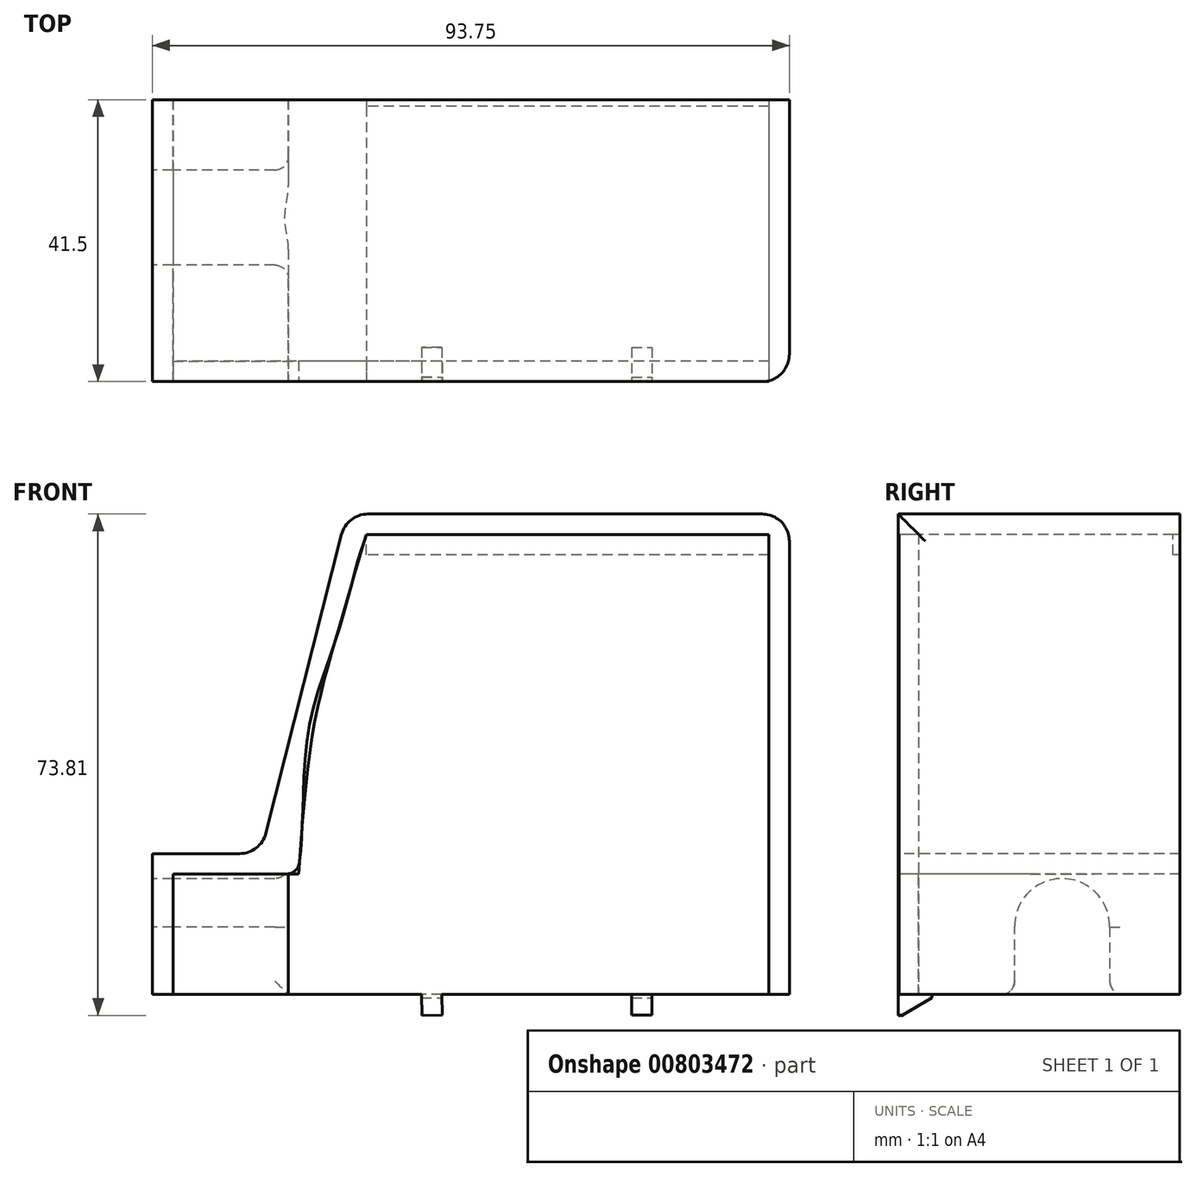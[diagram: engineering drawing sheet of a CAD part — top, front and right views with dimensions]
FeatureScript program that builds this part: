
annotation { "Feature Type Name" : "Feature", "Feature Type Description" : "" }
export const myFeature = defineFeature(function(context is Context, id is Id, definition is map)
    precondition{}
    {
        {
            var Q0;
            Q0=qCreatedBy(makeId("Front.planeOp"),FACE);
            var sketch = newSketch(context, id + "F0", { "sketchPlane" : qUnion([Q0])});
            skLineSegment(sketch, "E0", {"start": v(59.25, 24.1) * mm, "end": v(0, 24.1) * mm});
            skFitSpline(sketch, "E1", {"points": [v(0, 24.1) * mm, v(-4.07, 10.26) * mm, v(-7.71, -4.08) * mm, v(-10, -25.9) * mm], "startDerivative": vector(-13.66, -42.75) * mm, "endDerivative": vector(-4.48, -59.85) * mm});
            skLineSegment(sketch, "E2", {"start": v(59.26, -43.65) * mm, "end": v(-28.5, -43.65) * mm});
            skLineSegment(sketch, "E3", {"start": v(-28.5, -43.65) * mm, "end": v(-28.5, -25.9) * mm});
            skLineSegment(sketch, "E4", {"start": v(-28.5, -25.9) * mm, "end": v(-10, -25.9) * mm});
            skLineSegment(sketch, "E5", {"start": v(59.25, 24.1) * mm, "end": v(59.26, -43.65) * mm});
            skSolve(sketch);
        }
        {
            var Q0;
            Q0 = qSketchRegion(id + "F0", true);
            extrude(context, id + "F1", {"entities" : qUnion([Q0]), "oppositeDirection" : true, "depth" : 3 * mm, "offsetDistance" : 25 * mm});
        }
        {
            var Q0;
            Q0=makeQuery(id+"F0.imprint","IMPRINT",FACE,{"disambiguationData":[TD([[makeQuery(id+"F0.imprint","IMPRINT",EDGE,{"derivedFrom":sQuery(id+"F0.wireOp",EDGE,"E0")}),1.0]])]});
            var Q1;
            Q1 = qBodyType(qCreatedBy(id + "Fs2WI9H54nxdFtR_1" ,EDGE), BodyType.WIRE);
            cPlane(context, id + "F2", {"entities" : qUnion([Q0, Q1]), "cplaneType" : CPlaneType.OFFSET, "offset" : 0 * mm, "width" : 150 * mm, "height" : 150 * mm});
        }
        {
            var Q0;
            Q0=qCreatedBy(id+"F2.planeOp",FACE);
            var sketch = newSketch(context, id + "F3", { "sketchPlane" : qUnion([Q0])});
            skLineSegment(sketch, "E6.0.0", {"start": v(-28.5, -25.9) * mm, "end": v(-28.5, -43.65) * mm});
            skLineSegment(sketch, "E6.0.2", {"start": v(59.26, -43.65) * mm, "end": v(59.25, 24.1) * mm});
            skLineSegment(sketch, "E6.0.3", {"start": v(59.25, 24.1) * mm, "end": v(0, 24.1) * mm});
            skFitSpline(sketch, "E6.0.4", {"points": [v(0, 24.1) * mm, v(-1.4, 19.7) * mm, v(-4.08, 9.94) * mm, v(-8.4, -4.13) * mm, v(-9.43, -18.32) * mm, v(-10, -25.9) * mm]});
            skLineSegment(sketch, "E6.0.5", {"start": v(-10, -25.9) * mm, "end": v(-28.5, -25.9) * mm});
            skLineSegment(sketch, "E7", {"start": v(-28.5, -43.65) * mm, "end": v(-31.5, -43.65) * mm});
            skLineSegment(sketch, "E8", {"start": v(-31.5, -43.65) * mm, "end": v(-31.5, -22.9) * mm});
            skLineSegment(sketch, "E9", {"start": v(-31.5, -22.9) * mm, "end": v(-15.56, -22.9) * mm});
            skLineSegment(sketch, "E10", {"start": v(-15.56, -22.9) * mm, "end": v(-2.92, 27.1) * mm});
            skLineSegment(sketch, "E11", {"start": v(-2.92, 27.1) * mm, "end": v(62.26, 27.1) * mm});
            skLineSegment(sketch, "E12", {"start": v(62.26, 27.1) * mm, "end": v(62.26, -43.65) * mm});
            skLineSegment(sketch, "E13", {"start": v(62.26, -43.65) * mm, "end": v(59.26, -43.65) * mm});
            skSolve(sketch);
        }
        {
            var Q0;
            Q0 = qSketchRegion(id + "F3", true);
            extrude(context, id + "F4", {"entities" : qUnion([Q0]), "oppositeDirection" : true, "depth" : 41.5 * mm, "offsetDistance" : 25 * mm});
        }
        {
            var Q0;
            Q0=makeQuery(id+"F4.opExtrude","SWEPT_FACE",FACE,{"disambiguationData":[OSD([sQuery(id+"F3.wireOp",EDGE,"E8")])]});
            cPlane(context, id + "F5", {"entities" : qUnion([Q0]), "cplaneType" : CPlaneType.OFFSET, "offset" : 0 * mm, "width" : 150 * mm, "height" : 150 * mm});
        }
        {
            var Q0;
            Q0=qCreatedBy(id+"F5.planeOp",FACE);
            var sketch = newSketch(context, id + "F6", { "sketchPlane" : qUnion([Q0])});
            skArc(sketch, "E14", {"start": v(-17.15, -33.62) * mm, "mid": v(-24.19, -26.58) * mm, "end": v(-31.15, -33.7) * mm});
            skLineSegment(sketch, "E15", {"start": v(-17.15, -33.62) * mm, "end": v(-17.15, -53.22) * mm});
            skLineSegment(sketch, "E16", {"start": v(-31.15, -33.46) * mm, "end": v(-31.15, -53.02) * mm});
            skLineSegment(sketch, "E17", {"start": v(-31.15, -53.02) * mm, "end": v(-17.15, -53.22) * mm});
            skSolve(sketch);
        }
        {
            var Q0;
            Q0 = qSketchRegion(id + "F6", true);
            extrude(context, id + "F7", {"entities" : qUnion([Q0]), "operationType" : NewBodyOperationType.REMOVE, "oppositeDirection" : true, "depth" : 25 * mm, "offsetDistance" : 25 * mm});
        }
        {
            var Q0;
            Q0=makeQuery(id+"F4.opExtrude","SWEPT_FACE",FACE,{"disambiguationData":[OSD([sQuery(id+"F3.wireOp",EDGE,"E6.0.0")])]});
            cPlane(context, id + "F8", {"entities" : qUnion([Q0]), "cplaneType" : CPlaneType.OFFSET, "offset" : 0 * mm, "width" : 150 * mm, "height" : 150 * mm});
        }
        {
            var Q0;
            Q0=qCreatedBy(id+"F8.planeOp",FACE);
            var sketch = newSketch(context, id + "F9", { "sketchPlane" : qUnion([Q0])});
            skArc(sketch, "E18.0.0", {"start": v(17.15, -33.62) * mm, "mid": v(24.19, -26.58) * mm, "end": v(31.15, -33.7) * mm});
            skLineSegment(sketch, "E18.0.1", {"start": v(31.15, -33.7) * mm, "end": v(31.15, -43.65) * mm});
            skLineSegment(sketch, "E18.0.2", {"start": v(31.15, -43.65) * mm, "end": v(41.5, -43.65) * mm});
            skLineSegment(sketch, "E18.0.3", {"start": v(41.5, -43.65) * mm, "end": v(41.5, -25.9) * mm});
            skLineSegment(sketch, "E18.0.4", {"start": v(41.5, -25.9) * mm, "end": v(0, -25.9) * mm});
            skLineSegment(sketch, "E18.0.5", {"start": v(0, -25.9) * mm, "end": v(0, -43.65) * mm});
            skLineSegment(sketch, "E18.0.6", {"start": v(0, -43.65) * mm, "end": v(17.15, -43.65) * mm});
            skLineSegment(sketch, "E18.0.7", {"start": v(17.15, -43.65) * mm, "end": v(17.15, -33.62) * mm});
            skSolve(sketch);
        }
        {
            var Q0;
            Q0 = qSketchRegion(id + "F9", true);
            extrude(context, id + "F10", {"entities" : qUnion([Q0]), "depth" : 17 * mm, "offsetDistance" : 25 * mm});
        }
        {
            var Q0;
            Q0=makeQuery(id+"F0.imprint","IMPRINT",FACE,{"disambiguationData":[TD([[makeQuery(id+"F0.imprint","IMPRINT",EDGE,{"derivedFrom":sQuery(id+"F0.wireOp",EDGE,"E0")}),1.0]])]});
            var sketch = newSketch(context, id + "F11", { "sketchPlane" : qUnion([Q0])});
            skLineSegment(sketch, "E19", {"start": v(42.05, -43.65) * mm, "end": v(42.05, -46.65) * mm});
            skLineSegment(sketch, "E20", {"start": v(42.05, -46.65) * mm, "end": v(39.05, -46.65) * mm});
            skLineSegment(sketch, "E21", {"start": v(39.05, -46.65) * mm, "end": v(39.05, -43.7) * mm});
            skLineSegment(sketch, "E22", {"start": v(39.05, -43.7) * mm, "end": v(42.05, -43.65) * mm});
            skLineSegment(sketch, "E23", {"start": v(11.1, -43.65) * mm, "end": v(11.15, -46.65) * mm});
            skLineSegment(sketch, "E24", {"start": v(11.15, -46.65) * mm, "end": v(8.15, -46.7) * mm});
            skLineSegment(sketch, "E25", {"start": v(8.15, -46.7) * mm, "end": v(8.1, -43.65) * mm});
            skLineSegment(sketch, "E26", {"start": v(8.1, -43.65) * mm, "end": v(11.1, -43.65) * mm});
            skSolve(sketch);
        }
        {
            var Q0;
            Q0 = qSketchRegion(id + "F11", true);
            extrude(context, id + "F12", {"entities" : qUnion([Q0]), "operationType" : NewBodyOperationType.ADD, "oppositeDirection" : true, "depth" : 5 * mm, "offsetDistance" : 25 * mm});
        }
        {
            var Q0;
            Q0=makeQuery(id+"F12.opExtrude","SWEPT_FACE",FACE,{"disambiguationData":[OSD([sQuery(id+"F11.wireOp",EDGE,"E19")])]});
            var sketch = newSketch(context, id + "F13", { "sketchPlane" : qUnion([Q0])});
            skLineSegment(sketch, "E27", {"start": v(5, -44.15) * mm, "end": v(0.67, -46.65) * mm});
            skLineSegment(sketch, "E28", {"start": v(0.67, -46.65) * mm, "end": v(5, -46.65) * mm});
            skLineSegment(sketch, "E29", {"start": v(5, -46.65) * mm, "end": v(5, -44.15) * mm});
            skSolve(sketch);
        }
        {
            var Q0;
            Q0=makeQuery(id+"F13.imprint","IMPRINT",FACE,{"disambiguationData":[TD([[makeQuery(id+"F13.imprint","IMPRINT",EDGE,{"derivedFrom":sQuery(id+"F13.wireOp",EDGE,"E27")}),1.0]])]});
            extrude(context, id + "F14", {"entities" : qUnion([Q0]), "operationType" : NewBodyOperationType.REMOVE, "oppositeDirection" : true, "depth" : 70 * mm, "offsetDistance" : 25 * mm});
        }
        {
            var Q0;
            Q0=makeQuery(id+"F12.opExtrude","SWEPT_FACE",FACE,{"disambiguationData":[OSD([sQuery(id+"F11.wireOp",EDGE,"E23")])]});
            var sketch = newSketch(context, id + "F15", { "sketchPlane" : qUnion([Q0])});
            skLineSegment(sketch, "E30", {"start": v(5, -44.34) * mm, "end": v(0.67, -46.84) * mm});
            skLineSegment(sketch, "E31", {"start": v(0.67, -46.84) * mm, "end": v(5, -46.84) * mm});
            skLineSegment(sketch, "E32", {"start": v(5, -46.84) * mm, "end": v(5, -44.34) * mm});
            skSolve(sketch);
        }
        {
            var Q0;
            Q0 = qSketchRegion(id + "F15", true);
            extrude(context, id + "F16", {"entities" : qUnion([Q0]), "operationType" : NewBodyOperationType.REMOVE, "oppositeDirection" : true, "depth" : 25 * mm, "offsetDistance" : 25 * mm});
        }
        {
            var Q0;
            Q0=makeQuery(id+"F4.opExtrude","SWEPT_FACE",FACE,{"disambiguationData":[OSD([sQuery(id+"F3.wireOp",EDGE,"E6.0.3")])]});
            var sketch = newSketch(context, id + "F17", { "sketchPlane" : qUnion([Q0])});
            skLineSegment(sketch, "E33", {"start": v(59.25, -41.5) * mm, "end": v(59.25, -40.5) * mm});
            skLineSegment(sketch, "E34", {"start": v(59.25, -40.5) * mm, "end": v(0, -40.5) * mm});
            skLineSegment(sketch, "E35", {"start": v(0, -40.5) * mm, "end": v(0, -41.5) * mm});
            skLineSegment(sketch, "E36", {"start": v(0, -41.5) * mm, "end": v(59.25, -41.5) * mm});
            skSolve(sketch);
        }
        {
            var Q0;
            Q0=makeQuery(id+"F17.imprint","IMPRINT",FACE,{"disambiguationData":[TD([[makeQuery(id+"F17.imprint","IMPRINT",EDGE,{"derivedFrom":sQuery(id+"F17.wireOp",EDGE,"E33")}),1.0]])]});
            extrude(context, id + "F18", {"entities" : qUnion([Q0]), "operationType" : NewBodyOperationType.ADD, "depth" : 3 * mm, "offsetDistance" : 25 * mm});
        }
        {
            var Q0;
            Q0=makeQuery(id+"F4.opExtrude","SWEPT_EDGE",EDGE,{"disambiguationData":[OSD([sQuery(id+"F3.wireOp",EDGE,"E11"),sQuery(id+"F3.wireOp",EDGE,"E12")])]});
            var Q1;
            Q1=makeQuery(id+"F4.opExtrude","SWEPT_EDGE",EDGE,{"disambiguationData":[OSD([sQuery(id+"F3.wireOp",EDGE,"E10"),sQuery(id+"F3.wireOp",EDGE,"E11")])]});
            var Q2;
            Q2=makeQuery(id+"F4.opExtrude","SWEPT_EDGE",EDGE,{"disambiguationData":[OSD([sQuery(id+"F3.wireOp",EDGE,"E9"),sQuery(id+"F3.wireOp",EDGE,"E10")])]});
            var Q3;
            Q3=makeQuery(id+"F4.opExtrude","CAP_EDGE",EDGE,{"disambiguationData":[OSD([sQuery(id+"F3.wireOp",EDGE,"E12")])],"isStart":true});
            fillet(context, id + "F19", {"entities" : qUnion([Q0, Q1, Q2, Q3]), "radius" : 4 * mm, "tangentPropagation" : true, "allowEdgeOverflow" : false});
        }
        {
            var Q0;
            Q0=makeQuery(id+"F4.opExtrude","SWEPT_EDGE",EDGE,{"disambiguationData":[OSD([sQuery(id+"F3.wireOp",EDGE,"E6.0.4"),sQuery(id+"F3.wireOp",EDGE,"E6.0.5")])]});
            var Q1;
            Q1=makeQuery(id+"F10.opExtrude","CAP_EDGE",EDGE,{"disambiguationData":[OSD([sQuery(id+"F9.wireOp",EDGE,"E18.0.0")])],"isStart":false});
            var Q2;
            Q2=makeQuery(id+"F10.opExtrude","CAP_EDGE",EDGE,{"disambiguationData":[OSD([sQuery(id+"F9.wireOp",EDGE,"E18.0.7")])],"isStart":false});
            var Q3;
            Q3=makeQuery(id+"F10.opExtrude","CAP_EDGE",EDGE,{"disambiguationData":[OSD([sQuery(id+"F9.wireOp",EDGE,"E18.0.1")])],"isStart":false});
            var Q4;
            Q4=makeQuery(id+"F7.boolean.opBoolean","COPY",EDGE,{"derivedFrom":makeQuery(id+"F7.opExtrude","CAP_EDGE",EDGE,{"disambiguationData":[OSD([sQuery(id+"F6.wireOp",EDGE,"E15")])],"isStart":true})});
            var Q5;
            Q5=makeQuery(id+"F7.boolean.opBoolean","COPY",EDGE,{"derivedFrom":makeQuery(id+"F7.opExtrude","CAP_EDGE",EDGE,{"disambiguationData":[OSD([sQuery(id+"F6.wireOp",EDGE,"E14")])],"isStart":true})});
            var Q6;
            Q6=makeQuery(id+"F7.boolean.opBoolean","COPY",EDGE,{"derivedFrom":makeQuery(id+"F7.opExtrude","CAP_EDGE",EDGE,{"disambiguationData":[OSD([sQuery(id+"F6.wireOp",EDGE,"E16")])],"isStart":true})});
            var Q7;
            Q7=makeQuery(id+"F10.opExtrude","SWEPT_EDGE",EDGE,{"disambiguationData":[OSD([sQuery(id+"F9.wireOp",EDGE,"E18.0.1"),sQuery(id+"F9.wireOp",EDGE,"E18.0.2")])]});
            var Q8;
            Q8=makeQuery(id+"F10.opExtrude","SWEPT_EDGE",EDGE,{"disambiguationData":[OSD([sQuery(id+"F9.wireOp",EDGE,"E18.0.6"),sQuery(id+"F9.wireOp",EDGE,"E18.0.7")])]});
            var Q9;
            Q9=makeQuery(id+"F7.boolean.opBoolean","INTERSECT",EDGE,{"derivedFrom":[makeQuery(id+"F4.opExtrude","SWEPT_FACE",FACE,{"disambiguationData":[OSD([sQuery(id+"F3.wireOp",EDGE,"E7")])]}),makeQuery(id+"F7.opExtrude","SWEPT_FACE",FACE,{"disambiguationData":[OSD([sQuery(id+"F6.wireOp",EDGE,"E15")])]})]});
            var Q10;
            Q10=makeQuery(id+"F7.boolean.opBoolean","INTERSECT",EDGE,{"derivedFrom":[makeQuery(id+"F4.opExtrude","SWEPT_FACE",FACE,{"disambiguationData":[OSD([sQuery(id+"F3.wireOp",EDGE,"E7")])]}),makeQuery(id+"F7.opExtrude","SWEPT_FACE",FACE,{"disambiguationData":[OSD([sQuery(id+"F6.wireOp",EDGE,"E16")])]})]});
            var Q11;
            Q11=makeQuery(id+"F18.opExtrude","CAP_EDGE",EDGE,{"disambiguationData":[OSD([sQuery(id+"F17.wireOp",EDGE,"E34")])],"isStart":true});
            fillet(context, id + "F20", {"entities" : qUnion([Q0, Q1, Q2, Q3, Q4, Q5, Q6, Q7, Q8, Q9, Q10, Q11]), "radius" : 2 * mm, "tangentPropagation" : true, "allowEdgeOverflow" : false});
        }
    });
